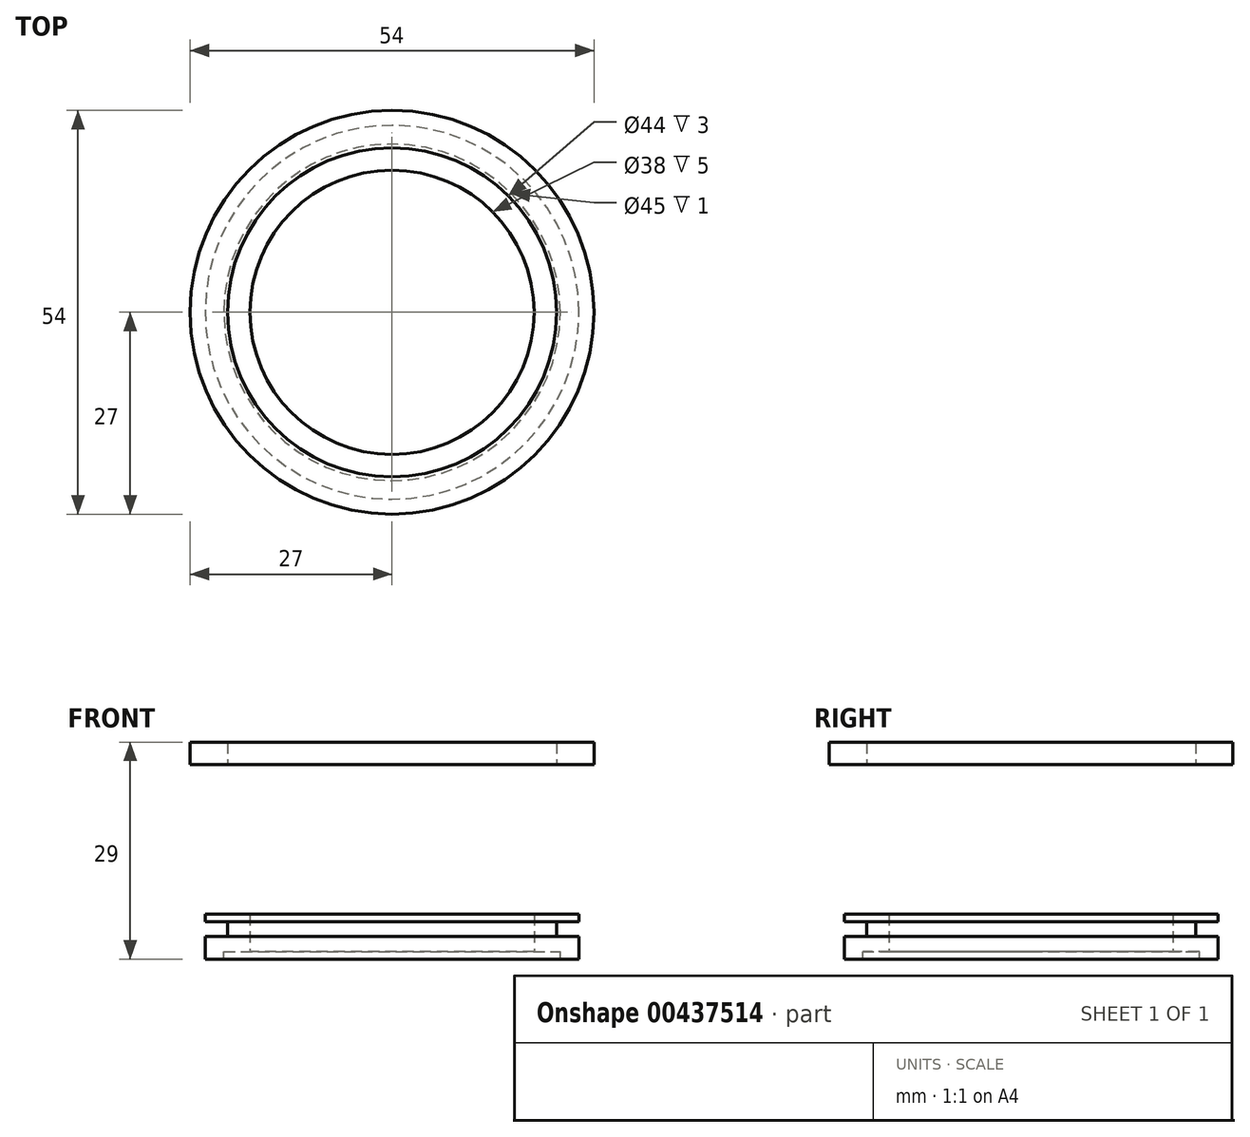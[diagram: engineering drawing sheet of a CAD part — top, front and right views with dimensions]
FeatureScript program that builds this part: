
annotation { "Feature Type Name" : "Feature", "Feature Type Description" : "" }
export const myFeature = defineFeature(function(context is Context, id is Id, definition is map)
    precondition{}
    {
        {
            var Q0;
            Q0=qCreatedBy(makeId("Top.planeOp"),FACE);
            var sketch = newSketch(context, id + "F0", { "sketchPlane" : qUnion([Q0])});
            skCircle(sketch, "E0", {"center": v(0, 0) * mm, "radius": 19 * mm});
            skCircle(sketch, "E1", {"center": v(0, 0) * mm, "radius": 22 * mm});
            skSolve(sketch);
        }
        {
            var Q0;
            Q0=makeQuery(id+"F0.imprint","IMPRINT",FACE,{"disambiguationData":[TD([[makeQuery(id+"F0.imprint","IMPRINT",EDGE,{"derivedFrom":sQuery(id+"F0.wireOp",EDGE,"E0")}),-1.0]])]});
            extrude(context, id + "F1", {"entities" : qUnion([Q0]), "depth" : 5 * mm});
        }
        {
            var Q0;
            Q0=makeQuery(id+"F1.opExtrude","CAP_FACE",FACE,{"disambiguationData":[OSD([sQuery(id+"F0.wireOp",EDGE,"E0"),sQuery(id+"F0.wireOp",EDGE,"E1")])],"isStart":false});
            var sketch = newSketch(context, id + "F2", { "sketchPlane" : qUnion([Q0])});
            skCircle(sketch, "E2", {"center": v(0, 0) * mm, "radius": 25 * mm});
            skCircle(sketch, "E3", {"center": v(0, 0) * mm, "radius": 19 * mm});
            skSolve(sketch);
        }
        {
            var Q0;
            Q0=makeQuery(id+"F2.imprint","IMPRINT",FACE,{"disambiguationData":[TD([[makeQuery(id+"F2.imprint","IMPRINT",EDGE,{"derivedFrom":sQuery(id+"F2.wireOp",EDGE,"E2")}),1.0]])]});
            extrude(context, id + "F3", {"entities" : qUnion([Q0]), "operationType" : NewBodyOperationType.ADD, "depth" : -1 * mm});
        }
        {
            var Q0;
            Q0=makeQuery(id+"F1.opExtrude","CAP_FACE",FACE,{"disambiguationData":[OSD([sQuery(id+"F0.wireOp",EDGE,"E0"),sQuery(id+"F0.wireOp",EDGE,"E1")])],"isStart":true});
            var sketch = newSketch(context, id + "F4", { "sketchPlane" : qUnion([Q0])});
            skCircle(sketch, "E4", {"center": v(0, 0) * mm, "radius": 21 * mm});
            skCircle(sketch, "E5", {"center": v(0, 0) * mm, "radius": 25 * mm});
            skSolve(sketch);
        }
        {
            var Q0;
            Q0=makeQuery(id+"F4.imprint","IMPRINT",FACE,{"disambiguationData":[TD([[makeQuery(id+"F4.imprint","IMPRINT",EDGE,{"derivedFrom":sQuery(id+"F4.wireOp",EDGE,"E5")}),1.0]])]});
            var Q1;
            Q1=makeQuery(id+"F4.imprint","IMPRINT",FACE,{"disambiguationData":[TD([[makeQuery(id+"F4.imprint","IMPRINT",EDGE,{"derivedFrom":sQuery(id+"F4.wireOp",EDGE,"E4")}),-1.0]])]});
            extrude(context, id + "F5", {"entities" : qUnion([Q0, Q1]), "operationType" : NewBodyOperationType.ADD, "depth" : 1 * mm});
        }
        {
            var Q0;
            Q0=makeQuery(id+"F4.imprint","IMPRINT",FACE,{"disambiguationData":[TD([[makeQuery(id+"F4.imprint","IMPRINT",EDGE,{"derivedFrom":sQuery(id+"F4.wireOp",EDGE,"E5")}),1.0]])]});
            extrude(context, id + "F6", {"entities" : qUnion([Q0]), "operationType" : NewBodyOperationType.ADD, "depth" : -2 * mm});
        }
        {
            var Q0;
            Q0=makeQuery(id+"F4.imprint","IMPRINT",FACE,{"disambiguationData":[TD([[makeQuery(id+"F4.imprint","IMPRINT",EDGE,{"derivedFrom":sQuery(id+"F4.wireOp",EDGE,"E4")}),1.0]])]});
            var sketch = newSketch(context, id + "F7", { "sketchPlane" : qUnion([Q0])});
            skCircle(sketch, "E6", {"center": v(0, 0) * mm, "radius": 22.5 * mm});
            skSolve(sketch);
        }
        {
            var Q0;
            Q0 = qSketchRegion(id + "F7", true);
            extrude(context, id + "F8", {"entities" : qUnion([Q0]), "operationType" : NewBodyOperationType.REMOVE, "depth" : 4 * mm});
        }
        {
            var Q0;
            Q0=qCreatedBy(makeId("Top.planeOp"),FACE);
            cPlane(context, id + "F9", {"entities" : qUnion([Q0]), "cplaneType" : CPlaneType.OFFSET, "offset" : 25 * mm, "width" : 150 * mm, "height" : 150 * mm});
        }
        {
            var Q0;
            Q0=qCreatedBy(id+"F9.planeOp",FACE);
            var sketch = newSketch(context, id + "F10", { "sketchPlane" : qUnion([Q0])});
            skCircle(sketch, "E7", {"center": v(0, 0) * mm, "radius": 22 * mm});
            skCircle(sketch, "E8", {"center": v(0, 0) * mm, "radius": 27 * mm});
            skSolve(sketch);
        }
        {
            var Q0;
            Q0=makeQuery(id+"F10.imprint","IMPRINT",FACE,{"disambiguationData":[TD([[makeQuery(id+"F10.imprint","IMPRINT",EDGE,{"derivedFrom":sQuery(id+"F10.wireOp",EDGE,"E7")}),-1.0]])]});
            extrude(context, id + "F11", {"entities" : qUnion([Q0]), "depth" : 3 * mm});
        }
    });
